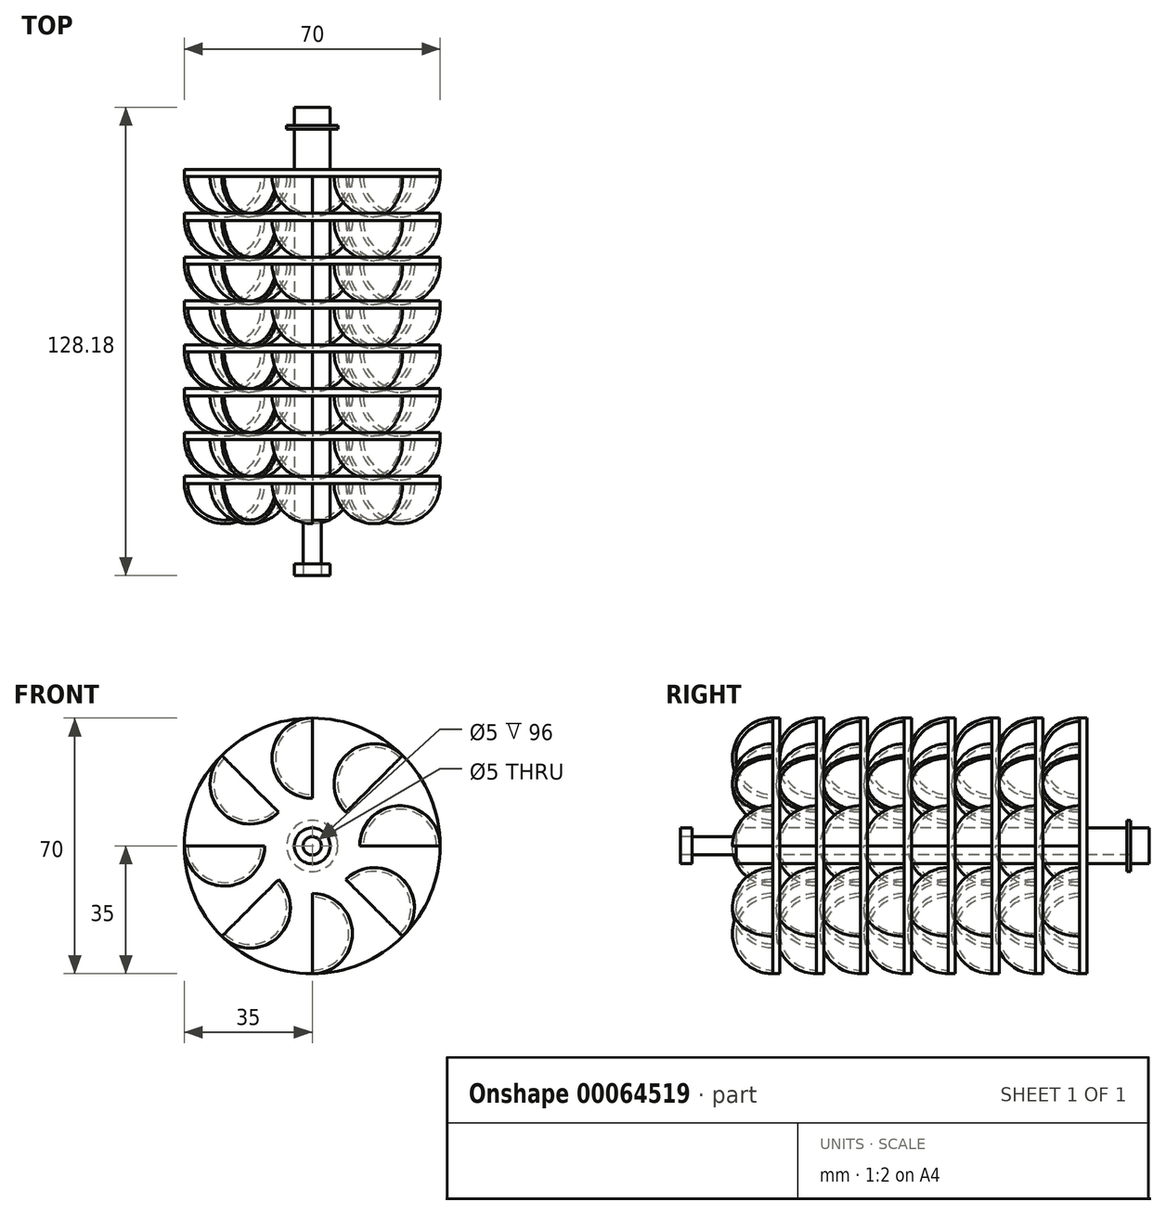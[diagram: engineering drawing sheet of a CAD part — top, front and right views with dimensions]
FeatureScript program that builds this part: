
annotation { "Feature Type Name" : "Feature", "Feature Type Description" : "" }
export const myFeature = defineFeature(function(context is Context, id is Id, definition is map)
    precondition{}
    {
        {
            var Q0;
            Q0=qCreatedBy(makeId("Right.planeOp"),FACE);
            var sketch = newSketch(context, id + "F0", { "sketchPlane" : qUnion([Q0])});
            skArc(sketch, "E0", {"start": v(0, 10) * mm, "mid": v(-7.07, 7.07) * mm, "end": v(-10, 0) * mm});
            skLineSegment(sketch, "E1", {"start": v(-10, 0) * mm, "end": v(0, 0) * mm});
            skLineSegment(sketch, "E2", {"start": v(0, 10) * mm, "end": v(0, 0) * mm});
            skArc(sketch, "E3", {"start": v(0, 11) * mm, "mid": v(-7.78, 7.78) * mm, "end": v(-11, 0) * mm});
            skLineSegment(sketch, "E4", {"start": v(0, 10) * mm, "end": v(0, 11) * mm});
            skLineSegment(sketch, "E5", {"start": v(-11, 0) * mm, "end": v(-10, 0) * mm});
            skSolve(sketch);
        }
        {
            var Q0;
            Q0=makeQuery(id+"F0.imprint","IMPRINT",FACE,{"disambiguationData":[TD([[makeQuery(id+"F0.imprint","IMPRINT",EDGE,{"derivedFrom":sQuery(id+"F0.wireOp",EDGE,"E0")}),-1.0]])]});
            var Q1;
            Q1=sQuery(id+"F0.wireOp",EDGE,"E0");
            var Q2;
            Q2=sQuery(id+"F0.wireOp",EDGE,"E1");
            revolve(context, id + "F1", {"entities" : qUnion([Q0]), "surfaceEntities" : qUnion([Q1]), "axis" : qUnion([Q2]), "revolveType" : RevolveType.TWO_DIRECTIONS, "angle" : 90 * degree, "angleBack" : 270 * degree});
        }
        {
            var Q0;
            Q0=makeQuery(id+"F1.opRevolve","SWEPT_BODY",BODY,{"disambiguationData":[OSD([sQuery(id+"F0.wireOp",EDGE,"E0"),sQuery(id+"F0.wireOp",EDGE,"E3"),sQuery(id+"F0.wireOp",EDGE,"E4"),sQuery(id+"F0.wireOp",EDGE,"E5")])]});
            transform(context, id + "F2", {"entities" : qUnion([Q0]), "transformType" : TransformType.TRANSLATION_3D, "dx" : 24 * mm, "dy" : 0 * mm, "dz" : 0 * mm, "makeCopy" : false});
        }
        {
            var Q0;
            Q0=qCreatedBy(makeId("Right.planeOp"),FACE);
            var sketch = newSketch(context, id + "F3", { "sketchPlane" : qUnion([Q0])});
            skLineSegment(sketch, "E6", {"start": v(-12, 0) * mm, "end": v(0, 0) * mm});
            skLineSegment(sketch, "E7", {"start": v(0, 0) * mm, "end": v(10, 0) * mm});
            skLineSegment(sketch, "E8", {"start": v(0, 0) * mm, "end": v(0, 35) * mm});
            skLineSegment(sketch, "E9.bottom", {"start": v(-2, 0) * mm, "end": v(0, 0) * mm});
            skLineSegment(sketch, "E9.top", {"start": v(-2, 35) * mm, "end": v(0, 35) * mm});
            skLineSegment(sketch, "E9.right", {"start": v(-2, 0) * mm, "end": v(-2, 35) * mm});
            skLineSegment(sketch, "E10", {"start": v(-24, 4.9) * mm, "end": v(0, 4.9) * mm});
            skLineSegment(sketch, "E11", {"start": v(0, 4.9) * mm, "end": v(10, 4.9) * mm});
            skLineSegment(sketch, "E12", {"start": v(-2, 4.9) * mm, "end": v(-2, 0) * mm});
            skLineSegment(sketch, "E13", {"start": v(0, 4.9) * mm, "end": v(0, 0) * mm});
            skLineSegment(sketch, "E14", {"start": v(22, 0) * mm, "end": v(34, 0) * mm});
            skLineSegment(sketch, "E15", {"start": v(34, 0) * mm, "end": v(46, 0) * mm});
            skLineSegment(sketch, "E16", {"start": v(-12, 0) * mm, "end": v(-24, 0) * mm});
            skLineSegment(sketch, "E17", {"start": v(-24, 0) * mm, "end": v(-36, 0) * mm});
            skLineSegment(sketch, "E18", {"start": v(-36, 0) * mm, "end": v(-48, 0) * mm});
            skLineSegment(sketch, "E19", {"start": v(10, 0) * mm, "end": v(22, 0) * mm});
            skLineSegment(sketch, "E20", {"start": v(-24, 4.9) * mm, "end": v(-24, 4.9) * mm});
            skLineSegment(sketch, "E21", {"start": v(10, 4.9) * mm, "end": v(22, 4.9) * mm});
            skLineSegment(sketch, "E22", {"start": v(-24, 4.9) * mm, "end": v(-36, 4.9) * mm});
            skLineSegment(sketch, "E23", {"start": v(-36, 0) * mm, "end": v(-36, 4.9) * mm});
            skLineSegment(sketch, "E24", {"start": v(46, 0) * mm, "end": v(65, 0) * mm});
            skLineSegment(sketch, "E25", {"start": v(65, 0) * mm, "end": v(77, 0) * mm});
            skLineSegment(sketch, "E26", {"start": v(-48, 0) * mm, "end": v(-60, 0) * mm});
            skLineSegment(sketch, "E27", {"start": v(-36, 0) * mm, "end": v(-36, 2.5) * mm});
            skLineSegment(sketch, "E28", {"start": v(-36, 2.5) * mm, "end": v(22, 2.5) * mm});
            skLineSegment(sketch, "E29", {"start": v(-36, 0) * mm, "end": v(-38, 0) * mm});
            skLineSegment(sketch, "E30", {"start": v(10, 4.9) * mm, "end": v(10, 0) * mm});
            skLineSegment(sketch, "E31", {"start": v(10, 0) * mm, "end": v(10, 35) * mm});
            skLineSegment(sketch, "E32", {"start": v(10, 35) * mm, "end": v(12, 35) * mm});
            skLineSegment(sketch, "E33", {"start": v(12, 35) * mm, "end": v(12, 0) * mm});
            skLineSegment(sketch, "E34", {"start": v(22, 0) * mm, "end": v(22, 35) * mm});
            skLineSegment(sketch, "E35", {"start": v(22, 35) * mm, "end": v(24, 35) * mm});
            skLineSegment(sketch, "E36", {"start": v(24, 35) * mm, "end": v(24, 0) * mm});
            skLineSegment(sketch, "E37", {"start": v(34, 0) * mm, "end": v(34, 35) * mm});
            skLineSegment(sketch, "E38", {"start": v(34, 35) * mm, "end": v(36, 35) * mm});
            skLineSegment(sketch, "E39", {"start": v(36, 35) * mm, "end": v(36, 0) * mm});
            skLineSegment(sketch, "E40", {"start": v(46, 0) * mm, "end": v(46, 35) * mm});
            skLineSegment(sketch, "E41", {"start": v(46, 35) * mm, "end": v(48, 35) * mm});
            skLineSegment(sketch, "E42", {"start": v(48, 35) * mm, "end": v(48, 0) * mm});
            skLineSegment(sketch, "E43", {"start": v(22, 4.9) * mm, "end": v(34, 4.9) * mm});
            skLineSegment(sketch, "E44", {"start": v(34, 4.9) * mm, "end": v(46, 4.9) * mm});
            skLineSegment(sketch, "E45", {"start": v(46, 4.9) * mm, "end": v(65, 4.9) * mm});
            skLineSegment(sketch, "E46", {"start": v(65, 4.9) * mm, "end": v(65, 0) * mm});
            skLineSegment(sketch, "E47", {"start": v(22, 2.5) * mm, "end": v(48, 2.5) * mm});
            skLineSegment(sketch, "E48", {"start": v(-12, 35) * mm, "end": v(-14, 35) * mm});
            skLineSegment(sketch, "E49", {"start": v(-14, 35) * mm, "end": v(-14, 0) * mm});
            skLineSegment(sketch, "E50", {"start": v(-24, 0) * mm, "end": v(-24, 35) * mm});
            skLineSegment(sketch, "E51", {"start": v(-24, 35) * mm, "end": v(-26, 35) * mm});
            skLineSegment(sketch, "E52", {"start": v(-26, 35) * mm, "end": v(-26, 0) * mm});
            skLineSegment(sketch, "E53", {"start": v(-36, 0) * mm, "end": v(-36, 35) * mm});
            skLineSegment(sketch, "E54", {"start": v(-36, 35) * mm, "end": v(-38, 35) * mm});
            skLineSegment(sketch, "E55", {"start": v(-38, 35) * mm, "end": v(-38, 0) * mm});
            skLineSegment(sketch, "E56", {"start": v(-36, 4.9) * mm, "end": v(-48, 4.9) * mm});
            skLineSegment(sketch, "E57", {"start": v(-48, 4.9) * mm, "end": v(-60, 4.9) * mm});
            skLineSegment(sketch, "E58", {"start": v(-60, 4.9) * mm, "end": v(-60, 0) * mm});
            skLineSegment(sketch, "E59", {"start": v(-36, 2.5) * mm, "end": v(-60, 2.5) * mm});
            skLineSegment(sketch, "E60", {"start": v(-60, 0) * mm, "end": v(-60, 2.5) * mm});
            skLineSegment(sketch, "E61", {"start": v(-2, 4.9) * mm, "end": v(0, 4.9) * mm});
            skLineSegment(sketch, "E62", {"start": v(0, 0) * mm, "end": v(-2, 0) * mm});
            skLineSegment(sketch, "E63", {"start": v(10, 0) * mm, "end": v(-2, 0) * mm});
            skLineSegment(sketch, "E64", {"start": v(10, 4.9) * mm, "end": v(-2, 4.9) * mm});
            skLineSegment(sketch, "E65", {"start": v(22, 2.5) * mm, "end": v(12, 2.5) * mm});
            skLineSegment(sketch, "E66", {"start": v(-2, 4.9) * mm, "end": v(10, 4.9) * mm});
            skLineSegment(sketch, "E67", {"start": v(-60, 4.9) * mm, "end": v(-63.18, 4.9) * mm});
            skLineSegment(sketch, "E68", {"start": v(-63.18, 4.9) * mm, "end": v(-63.18, 0) * mm});
            skLineSegment(sketch, "E69", {"start": v(-63.18, 0) * mm, "end": v(-60, 0) * mm});
            skLineSegment(sketch, "E70", {"start": v(-63.18, 0) * mm, "end": v(-63.18, 2.5) * mm});
            skLineSegment(sketch, "E71", {"start": v(60, 0) * mm, "end": v(60, 7) * mm});
            skLineSegment(sketch, "E72", {"start": v(60, 7) * mm, "end": v(59, 7) * mm});
            skLineSegment(sketch, "E73", {"start": v(59, 0) * mm, "end": v(59, 7) * mm});
            skLineSegment(sketch, "E74", {"start": v(-12, 35) * mm, "end": v(-12, 0) * mm});
            skPoint(sketch, "E75", {"position": v(65, 2.5) * mm});
            skLineSegment(sketch, "E76", {"start": v(48, 2.5) * mm, "end": v(65, 2.5) * mm});
            skLineSegment(sketch, "E77", {"start": v(65, 2.5) * mm, "end": v(65, 0) * mm});
            skLineSegment(sketch, "E78", {"start": v(-60, 2.5) * mm, "end": v(-63.18, 2.5) * mm});
            skLineSegment(sketch, "E79", {"start": v(-60, 0) * mm, "end": v(-38, 0) * mm});
            skLineSegment(sketch, "E80", {"start": v(-60, 4.9) * mm, "end": v(-36, 4.9) * mm});
            skLineSegment(sketch, "E81", {"start": v(-60, 0) * mm, "end": v(-36, 0) * mm});
            skLineSegment(sketch, "E82", {"start": v(-48, 4.9) * mm, "end": v(-48, 0) * mm});
            skSolve(sketch);
        }
        {
            var Q0;
            {var subQ5=sQuery(id+"F3.wireOp",EDGE,"E22");var subQ7=makeQuery(id+"F3.imprint","IMPRINT",VERTEX,{"derivedFrom":subQ5});Q0=makeQuery(id+"F3.imprint","IMPRINT",FACE,{"disambiguationData":[TD([[makeQuery(id+"F3.imprint","IMPRINT",EDGE,{"disambiguationData":[TD([[subQ7,-1.0]])],"derivedFrom":subQ5}),1.0]])]});}
            var Q1;
            {var subQ3=sQuery(id+"F3.wireOp",EDGE,"E51");Q1=makeQuery(id+"F3.imprint","IMPRINT",FACE,{"disambiguationData":[TD([[makeQuery(id+"F3.imprint","IMPRINT",EDGE,{"derivedFrom":subQ3}),1.0]])]});}
            var Q2;
            {var subQ0=sQuery(id+"F3.wireOp",EDGE,"E50");var subQ5=sQuery(id+"F3.wireOp",EDGE,"E28");var subQ6=makeQuery(id+"F3.imprint","INTERSECT",VERTEX,{"derivedFrom":[subQ5,subQ0]});Q2=makeQuery(id+"F3.imprint","IMPRINT",FACE,{"disambiguationData":[TD([[makeQuery(id+"F3.imprint","IMPRINT",EDGE,{"disambiguationData":[TD([[subQ6,-1.0]])],"derivedFrom":subQ5}),1.0]])]});}
            var Q3;
            {var subQ0=sQuery(id+"F3.wireOp",EDGE,"E49");var subQ1=sQuery(id+"F3.wireOp",EDGE,"E10");var subQ2=makeQuery(id+"F3.imprint","INTERSECT",VERTEX,{"derivedFrom":[subQ1,subQ0]});Q3=makeQuery(id+"F3.imprint","IMPRINT",FACE,{"disambiguationData":[TD([[makeQuery(id+"F3.imprint","IMPRINT",EDGE,{"disambiguationData":[TD([[subQ2,-1.0]])],"derivedFrom":subQ1}),-1.0]])]});}
            var Q4;
            {var subQ5=sQuery(id+"F3.wireOp",EDGE,"E48");Q4=makeQuery(id+"F3.imprint","IMPRINT",FACE,{"disambiguationData":[TD([[makeQuery(id+"F3.imprint","IMPRINT",EDGE,{"derivedFrom":subQ5}),1.0]])]});}
            var Q5;
            {var subQ0=sQuery(id+"F3.wireOp",EDGE,"E12");var subQ5=sQuery(id+"F3.wireOp",EDGE,"E28");var subQ6=makeQuery(id+"F3.imprint","INTERSECT",VERTEX,{"derivedFrom":[subQ0,subQ5]});Q5=makeQuery(id+"F3.imprint","IMPRINT",FACE,{"disambiguationData":[TD([[makeQuery(id+"F3.imprint","IMPRINT",EDGE,{"disambiguationData":[TD([[subQ6,1.0]])],"derivedFrom":subQ5}),1.0]])]});}
            var Q6;
            {var subQ1=sQuery(id+"F3.wireOp",EDGE,"E42");var subQ3=sQuery(id+"F3.wireOp",EDGE,"E45");var subQ4=makeQuery(id+"F3.imprint","INTERSECT",VERTEX,{"derivedFrom":[subQ1,subQ3]});Q6=makeQuery(id+"F3.imprint","IMPRINT",FACE,{"disambiguationData":[TD([[makeQuery(id+"F3.imprint","IMPRINT",EDGE,{"disambiguationData":[TD([[subQ4,-1.0]])],"derivedFrom":subQ3}),-1.0]])]});}
            var Q7;
            {var subQ1=sQuery(id+"F3.wireOp",EDGE,"E40");var subQ3=sQuery(id+"F3.wireOp",EDGE,"E47");var subQ4=makeQuery(id+"F3.imprint","INTERSECT",VERTEX,{"derivedFrom":[subQ1,subQ3]});Q7=makeQuery(id+"F3.imprint","IMPRINT",FACE,{"disambiguationData":[TD([[makeQuery(id+"F3.imprint","IMPRINT",EDGE,{"disambiguationData":[TD([[subQ4,-1.0]])],"derivedFrom":subQ1}),-1.0]])]});}
            var Q8;
            {var subQ0=sQuery(id+"F3.wireOp",EDGE,"E41");Q8=makeQuery(id+"F3.imprint","IMPRINT",FACE,{"disambiguationData":[TD([[makeQuery(id+"F3.imprint","IMPRINT",EDGE,{"derivedFrom":subQ0}),-1.0]])]});}
            var Q9;
            {var subQ0=sQuery(id+"F3.wireOp",EDGE,"E44");var subQ1=sQuery(id+"F3.wireOp",EDGE,"E39");var subQ2=makeQuery(id+"F3.imprint","INTERSECT",VERTEX,{"derivedFrom":[subQ1,subQ0]});Q9=makeQuery(id+"F3.imprint","IMPRINT",FACE,{"disambiguationData":[TD([[makeQuery(id+"F3.imprint","IMPRINT",EDGE,{"disambiguationData":[TD([[subQ2,-1.0]])],"derivedFrom":subQ1}),1.0]])]});}
            var Q10;
            {var subQ0=sQuery(id+"F3.wireOp",EDGE,"E44");var subQ5=sQuery(id+"F3.wireOp",EDGE,"E39");var subQ6=makeQuery(id+"F3.imprint","INTERSECT",VERTEX,{"derivedFrom":[subQ5,subQ0]});Q10=makeQuery(id+"F3.imprint","IMPRINT",FACE,{"disambiguationData":[TD([[makeQuery(id+"F3.imprint","IMPRINT",EDGE,{"disambiguationData":[TD([[subQ6,-1.0]])],"derivedFrom":subQ5}),-1.0]])]});}
            var Q11;
            {var subQ0=sQuery(id+"F3.wireOp",EDGE,"E38");Q11=makeQuery(id+"F3.imprint","IMPRINT",FACE,{"disambiguationData":[TD([[makeQuery(id+"F3.imprint","IMPRINT",EDGE,{"derivedFrom":subQ0}),-1.0]])]});}
            var Q12;
            {var subQ0=sQuery(id+"F3.wireOp",EDGE,"E43");var subQ1=sQuery(id+"F3.wireOp",EDGE,"E36");var subQ2=makeQuery(id+"F3.imprint","INTERSECT",VERTEX,{"derivedFrom":[subQ1,subQ0]});Q12=makeQuery(id+"F3.imprint","IMPRINT",FACE,{"disambiguationData":[TD([[makeQuery(id+"F3.imprint","IMPRINT",EDGE,{"disambiguationData":[TD([[subQ2,-1.0]])],"derivedFrom":subQ1}),1.0]])]});}
            var Q13;
            {var subQ0=sQuery(id+"F3.wireOp",EDGE,"E43");var subQ5=sQuery(id+"F3.wireOp",EDGE,"E36");var subQ7=makeQuery(id+"F3.imprint","INTERSECT",VERTEX,{"derivedFrom":[subQ5,subQ0]});Q13=makeQuery(id+"F3.imprint","IMPRINT",FACE,{"disambiguationData":[TD([[makeQuery(id+"F3.imprint","IMPRINT",EDGE,{"disambiguationData":[TD([[subQ7,-1.0]])],"derivedFrom":subQ5}),-1.0]])]});}
            var Q14;
            {var subQ3=sQuery(id+"F3.wireOp",EDGE,"E35");Q14=makeQuery(id+"F3.imprint","IMPRINT",FACE,{"disambiguationData":[TD([[makeQuery(id+"F3.imprint","IMPRINT",EDGE,{"derivedFrom":subQ3}),-1.0]])]});}
            var Q15;
            {var subQ5=sQuery(id+"F3.wireOp",EDGE,"E65");Q15=makeQuery(id+"F3.imprint","IMPRINT",FACE,{"disambiguationData":[TD([[makeQuery(id+"F3.imprint","IMPRINT",EDGE,{"derivedFrom":subQ5}),-1.0]])]});}
            var Q16;
            {var subQ1=sQuery(id+"F3.wireOp",EDGE,"E21");var subQ3=sQuery(id+"F3.wireOp",EDGE,"E33");var subQ4=makeQuery(id+"F3.imprint","INTERSECT",VERTEX,{"derivedFrom":[subQ1,subQ3]});Q16=makeQuery(id+"F3.imprint","IMPRINT",FACE,{"disambiguationData":[TD([[makeQuery(id+"F3.imprint","IMPRINT",EDGE,{"disambiguationData":[TD([[subQ4,1.0]])],"derivedFrom":subQ1}),-1.0]])]});}
            var Q17;
            {var subQ5=sQuery(id+"F3.wireOp",EDGE,"E32");Q17=makeQuery(id+"F3.imprint","IMPRINT",FACE,{"disambiguationData":[TD([[makeQuery(id+"F3.imprint","IMPRINT",EDGE,{"derivedFrom":subQ5}),-1.0]])]});}
            var Q18;
            {var subQ1=sQuery(id+"F3.wireOp",EDGE,"E13");var subQ3=sQuery(id+"F3.wireOp",EDGE,"E28");var subQ4=makeQuery(id+"F3.imprint","INTERSECT",VERTEX,{"derivedFrom":[subQ1,subQ3]});Q18=makeQuery(id+"F3.imprint","IMPRINT",FACE,{"disambiguationData":[TD([[makeQuery(id+"F3.imprint","IMPRINT",EDGE,{"disambiguationData":[TD([[subQ4,-1.0]])],"derivedFrom":subQ3}),1.0]])]});}
            var Q19;
            {var subQ1=sQuery(id+"F3.wireOp",EDGE,"E12");var subQ3=sQuery(id+"F3.wireOp",EDGE,"E28");var subQ4=makeQuery(id+"F3.imprint","INTERSECT",VERTEX,{"derivedFrom":[subQ1,subQ3]});Q19=makeQuery(id+"F3.imprint","IMPRINT",FACE,{"disambiguationData":[TD([[makeQuery(id+"F3.imprint","IMPRINT",EDGE,{"disambiguationData":[TD([[subQ4,-1.0]])],"derivedFrom":subQ3}),1.0]])]});}
            var Q20;
            Q20=makeQuery(id+"F3.imprint","IMPRINT",FACE,{"disambiguationData":[TD([[makeQuery(id+"F3.imprint","IMPRINT",EDGE,{"derivedFrom":sQuery(id+"F3.wireOp",EDGE,"E9.top")}),-1.0]])]});
            var Q21;
            {var subQ0=sQuery(id+"F3.wireOp",EDGE,"E46");Q21=makeQuery(id+"F3.imprint","IMPRINT",FACE,{"disambiguationData":[TD([[makeQuery(id+"F3.imprint","IMPRINT",EDGE,{"derivedFrom":subQ0}),-1.0]])]});}
            var Q22;
            {var subQ0=sQuery(id+"F3.wireOp",EDGE,"E73");var subQ1=sQuery(id+"F3.wireOp",EDGE,"E45");var subQ2=makeQuery(id+"F3.imprint","INTERSECT",VERTEX,{"derivedFrom":[subQ1,subQ0]});Q22=makeQuery(id+"F3.imprint","IMPRINT",FACE,{"disambiguationData":[TD([[makeQuery(id+"F3.imprint","IMPRINT",EDGE,{"disambiguationData":[TD([[subQ2,-1.0]])],"derivedFrom":subQ1}),-1.0]])]});}
            var Q23;
            {var subQ5=sQuery(id+"F3.wireOp",EDGE,"E72");Q23=makeQuery(id+"F3.imprint","IMPRINT",FACE,{"disambiguationData":[TD([[makeQuery(id+"F3.imprint","IMPRINT",EDGE,{"derivedFrom":subQ5}),1.0]])]});}
            var Q24;
            {var subQ3=sQuery(id+"F3.wireOp",EDGE,"E82");var subQ5=sQuery(id+"F3.wireOp",EDGE,"E80");var subQ7=makeQuery(id+"F3.imprint","INTERSECT",VERTEX,{"derivedFrom":[subQ5,subQ3]});Q24=makeQuery(id+"F3.imprint","IMPRINT",FACE,{"disambiguationData":[TD([[makeQuery(id+"F3.imprint","IMPRINT",EDGE,{"disambiguationData":[TD([[subQ7,-1.0]])],"derivedFrom":subQ3}),-1.0]])]});}
            var Q25;
            {var subQ3=sQuery(id+"F3.wireOp",EDGE,"E82");var subQ5=sQuery(id+"F3.wireOp",EDGE,"E80");var subQ7=makeQuery(id+"F3.imprint","INTERSECT",VERTEX,{"derivedFrom":[subQ5,subQ3]});Q25=makeQuery(id+"F3.imprint","IMPRINT",FACE,{"disambiguationData":[TD([[makeQuery(id+"F3.imprint","IMPRINT",EDGE,{"disambiguationData":[TD([[subQ7,-1.0]])],"derivedFrom":subQ3}),-1.0]])]});}
            var Q26;
            {var subQ2=sQuery(id+"F3.wireOp",EDGE,"E67");Q26=makeQuery(id+"F3.imprint","IMPRINT",FACE,{"disambiguationData":[TD([[makeQuery(id+"F3.imprint","IMPRINT",EDGE,{"derivedFrom":subQ2}),1.0]])]});}
            var Q27;
            {var subQ0=sQuery(id+"F3.wireOp",EDGE,"E80");var subQ1=sQuery(id+"F3.wireOp",EDGE,"E55");var subQ2=makeQuery(id+"F3.imprint","INTERSECT",VERTEX,{"derivedFrom":[subQ1,subQ0]});Q27=makeQuery(id+"F3.imprint","IMPRINT",FACE,{"disambiguationData":[TD([[makeQuery(id+"F3.imprint","IMPRINT",EDGE,{"disambiguationData":[TD([[subQ2,-1.0]])],"derivedFrom":subQ1}),-1.0]])]});}
            var Q28;
            {var subQ0=sQuery(id+"F3.wireOp",EDGE,"E80");var subQ5=sQuery(id+"F3.wireOp",EDGE,"E55");var subQ6=makeQuery(id+"F3.imprint","INTERSECT",VERTEX,{"derivedFrom":[subQ5,subQ0]});Q28=makeQuery(id+"F3.imprint","IMPRINT",FACE,{"disambiguationData":[TD([[makeQuery(id+"F3.imprint","IMPRINT",EDGE,{"disambiguationData":[TD([[subQ6,-1.0]])],"derivedFrom":subQ5}),1.0]])]});}
            var Q29;
            {var subQ3=sQuery(id+"F3.wireOp",EDGE,"E54");Q29=makeQuery(id+"F3.imprint","IMPRINT",FACE,{"disambiguationData":[TD([[makeQuery(id+"F3.imprint","IMPRINT",EDGE,{"derivedFrom":subQ3}),1.0]])]});}
            var Q30;
            {var subQ1=sQuery(id+"F3.wireOp",EDGE,"E22");var subQ3=sQuery(id+"F3.wireOp",EDGE,"E52");var subQ4=makeQuery(id+"F3.imprint","INTERSECT",VERTEX,{"derivedFrom":[subQ1,subQ3]});Q30=makeQuery(id+"F3.imprint","IMPRINT",FACE,{"disambiguationData":[TD([[makeQuery(id+"F3.imprint","IMPRINT",EDGE,{"disambiguationData":[TD([[subQ4,-1.0]])],"derivedFrom":subQ3}),-1.0]])]});}
            var Q31;
            Q31=sQuery(id+"F3.wireOp",EDGE,"E6");
            revolve(context, id + "F4", {"entities" : qUnion([Q0, Q1, Q2, Q3, Q4, Q5, Q6, Q7, Q8, Q9, Q10, Q11, Q12, Q13, Q14, Q15, Q16, Q17, Q18, Q19, Q20, Q21, Q22, Q23, Q24, Q25, Q26, Q27, Q28, Q29, Q30]), "axis" : qUnion([Q31]), "revolveType" : RevolveType.FULL});
        }
        {
            var Q0;
            Q0=makeQuery(id+"F1.opRevolve","SWEPT_BODY",BODY,{"disambiguationData":[OSD([sQuery(id+"F0.wireOp",EDGE,"E0"),sQuery(id+"F0.wireOp",EDGE,"E3"),sQuery(id+"F0.wireOp",EDGE,"E4"),sQuery(id+"F0.wireOp",EDGE,"E5")])]});
            var Q1;
            Q1=sQuery(id+"F3.wireOp",EDGE,"E6");
            transform(context, id + "F5", {"entities" : qUnion([Q0]), "transformType" : TransformType.ROTATION, "transformAxis" : qUnion([Q1]), "angle" : 90 * degree, "makeCopy" : true});
        }
        {
            var Q0;
            Q0=makeQuery(id+"F1.opRevolve","SWEPT_BODY",BODY,{"disambiguationData":[OSD([sQuery(id+"F0.wireOp",EDGE,"E0"),sQuery(id+"F0.wireOp",EDGE,"E3"),sQuery(id+"F0.wireOp",EDGE,"E4"),sQuery(id+"F0.wireOp",EDGE,"E5")])]});
            var Q1;
            Q1=makeQuery(id+"F5.opPattern","COPY",BODY,{"derivedFrom":makeQuery(id+"F1.opRevolve","SWEPT_BODY",BODY,{"disambiguationData":[OSD([sQuery(id+"F0.wireOp",EDGE,"E0"),sQuery(id+"F0.wireOp",EDGE,"E3"),sQuery(id+"F0.wireOp",EDGE,"E4"),sQuery(id+"F0.wireOp",EDGE,"E5")])]}),"instanceName":"1"});
            var Q2;
            Q2=sQuery(id+"F3.wireOp",EDGE,"E7");
            transform(context, id + "F6", {"entities" : qUnion([Q0, Q1]), "transformType" : TransformType.ROTATION, "transformAxis" : qUnion([Q2]), "angle" : 180 * degree, "makeCopy" : true});
        }
        {
            var Q0;
            Q0=makeQuery(id+"F1.opRevolve","SWEPT_BODY",BODY,{"disambiguationData":[OSD([sQuery(id+"F0.wireOp",EDGE,"E0"),sQuery(id+"F0.wireOp",EDGE,"E3"),sQuery(id+"F0.wireOp",EDGE,"E4"),sQuery(id+"F0.wireOp",EDGE,"E5")])]});
            var Q1;
            Q1=makeQuery(id+"F6.opPattern","COPY",BODY,{"derivedFrom":makeQuery(id+"F5.opPattern","COPY",BODY,{"derivedFrom":makeQuery(id+"F1.opRevolve","SWEPT_BODY",BODY,{"disambiguationData":[OSD([sQuery(id+"F0.wireOp",EDGE,"E0"),sQuery(id+"F0.wireOp",EDGE,"E3"),sQuery(id+"F0.wireOp",EDGE,"E4"),sQuery(id+"F0.wireOp",EDGE,"E5")])]}),"instanceName":"1"}),"instanceName":"1"});
            var Q2;
            Q2=makeQuery(id+"F6.opPattern","COPY",BODY,{"derivedFrom":makeQuery(id+"F1.opRevolve","SWEPT_BODY",BODY,{"disambiguationData":[OSD([sQuery(id+"F0.wireOp",EDGE,"E0"),sQuery(id+"F0.wireOp",EDGE,"E3"),sQuery(id+"F0.wireOp",EDGE,"E4"),sQuery(id+"F0.wireOp",EDGE,"E5")])]}),"instanceName":"1"});
            var Q3;
            Q3=makeQuery(id+"F5.opPattern","COPY",BODY,{"derivedFrom":makeQuery(id+"F1.opRevolve","SWEPT_BODY",BODY,{"disambiguationData":[OSD([sQuery(id+"F0.wireOp",EDGE,"E0"),sQuery(id+"F0.wireOp",EDGE,"E3"),sQuery(id+"F0.wireOp",EDGE,"E4"),sQuery(id+"F0.wireOp",EDGE,"E5")])]}),"instanceName":"1"});
            var Q4;
            Q4=sQuery(id+"F3.wireOp",EDGE,"E25");
            transform(context, id + "F7", {"entities" : qUnion([Q0, Q1, Q2, Q3]), "transformType" : TransformType.ROTATION, "transformAxis" : qUnion([Q4]), "angle" : 45 * degree, "makeCopy" : true});
        }
        {
            var Q0;
            Q0=makeQuery(id+"F1.opRevolve","SWEPT_BODY",BODY,{"disambiguationData":[OSD([sQuery(id+"F0.wireOp",EDGE,"E0"),sQuery(id+"F0.wireOp",EDGE,"E3"),sQuery(id+"F0.wireOp",EDGE,"E4"),sQuery(id+"F0.wireOp",EDGE,"E5")])]});
            var Q1;
            Q1=makeQuery(id+"F7.opPattern","COPY",BODY,{"derivedFrom":makeQuery(id+"F1.opRevolve","SWEPT_BODY",BODY,{"disambiguationData":[OSD([sQuery(id+"F0.wireOp",EDGE,"E0"),sQuery(id+"F0.wireOp",EDGE,"E3"),sQuery(id+"F0.wireOp",EDGE,"E4"),sQuery(id+"F0.wireOp",EDGE,"E5")])]}),"instanceName":"1"});
            var Q2;
            Q2=makeQuery(id+"F5.opPattern","COPY",BODY,{"derivedFrom":makeQuery(id+"F1.opRevolve","SWEPT_BODY",BODY,{"disambiguationData":[OSD([sQuery(id+"F0.wireOp",EDGE,"E0"),sQuery(id+"F0.wireOp",EDGE,"E3"),sQuery(id+"F0.wireOp",EDGE,"E4"),sQuery(id+"F0.wireOp",EDGE,"E5")])]}),"instanceName":"1"});
            var Q3;
            Q3=makeQuery(id+"F7.opPattern","COPY",BODY,{"derivedFrom":makeQuery(id+"F5.opPattern","COPY",BODY,{"derivedFrom":makeQuery(id+"F1.opRevolve","SWEPT_BODY",BODY,{"disambiguationData":[OSD([sQuery(id+"F0.wireOp",EDGE,"E0"),sQuery(id+"F0.wireOp",EDGE,"E3"),sQuery(id+"F0.wireOp",EDGE,"E4"),sQuery(id+"F0.wireOp",EDGE,"E5")])]}),"instanceName":"1"}),"instanceName":"1"});
            var Q4;
            Q4=makeQuery(id+"F6.opPattern","COPY",BODY,{"derivedFrom":makeQuery(id+"F1.opRevolve","SWEPT_BODY",BODY,{"disambiguationData":[OSD([sQuery(id+"F0.wireOp",EDGE,"E0"),sQuery(id+"F0.wireOp",EDGE,"E3"),sQuery(id+"F0.wireOp",EDGE,"E4"),sQuery(id+"F0.wireOp",EDGE,"E5")])]}),"instanceName":"1"});
            var Q5;
            Q5=makeQuery(id+"F7.opPattern","COPY",BODY,{"derivedFrom":makeQuery(id+"F6.opPattern","COPY",BODY,{"derivedFrom":makeQuery(id+"F1.opRevolve","SWEPT_BODY",BODY,{"disambiguationData":[OSD([sQuery(id+"F0.wireOp",EDGE,"E0"),sQuery(id+"F0.wireOp",EDGE,"E3"),sQuery(id+"F0.wireOp",EDGE,"E4"),sQuery(id+"F0.wireOp",EDGE,"E5")])]}),"instanceName":"1"}),"instanceName":"1"});
            var Q6;
            Q6=makeQuery(id+"F6.opPattern","COPY",BODY,{"derivedFrom":makeQuery(id+"F5.opPattern","COPY",BODY,{"derivedFrom":makeQuery(id+"F1.opRevolve","SWEPT_BODY",BODY,{"disambiguationData":[OSD([sQuery(id+"F0.wireOp",EDGE,"E0"),sQuery(id+"F0.wireOp",EDGE,"E3"),sQuery(id+"F0.wireOp",EDGE,"E4"),sQuery(id+"F0.wireOp",EDGE,"E5")])]}),"instanceName":"1"}),"instanceName":"1"});
            var Q7;
            Q7=makeQuery(id+"F7.opPattern","COPY",BODY,{"derivedFrom":makeQuery(id+"F6.opPattern","COPY",BODY,{"derivedFrom":makeQuery(id+"F5.opPattern","COPY",BODY,{"derivedFrom":makeQuery(id+"F1.opRevolve","SWEPT_BODY",BODY,{"disambiguationData":[OSD([sQuery(id+"F0.wireOp",EDGE,"E0"),sQuery(id+"F0.wireOp",EDGE,"E3"),sQuery(id+"F0.wireOp",EDGE,"E4"),sQuery(id+"F0.wireOp",EDGE,"E5")])]}),"instanceName":"1"}),"instanceName":"1"}),"instanceName":"1"});
            var Q8;
            Q8=sQuery(id+"F3.wireOp",VERTEX,"E8.start");
            var Q9;
            Q9=sQuery(id+"F3.wireOp",VERTEX,"E62.end");
            transform(context, id + "F8", {"entities" : qUnion([Q0, Q1, Q2, Q3, Q4, Q5, Q6, Q7]), "transformType" : TransformType.TRANSLATION_ENTITY, "oppositeDirectionEntity" : false, "transformLine" : qUnion([Q8, Q9]), "makeCopy" : false});
        }
        {
            var Q0;
            Q0=makeQuery(id+"F7.opPattern","COPY",BODY,{"derivedFrom":makeQuery(id+"F5.opPattern","COPY",BODY,{"derivedFrom":makeQuery(id+"F1.opRevolve","SWEPT_BODY",BODY,{"disambiguationData":[OSD([sQuery(id+"F0.wireOp",EDGE,"E0"),sQuery(id+"F0.wireOp",EDGE,"E3"),sQuery(id+"F0.wireOp",EDGE,"E4"),sQuery(id+"F0.wireOp",EDGE,"E5")])]}),"instanceName":"1"}),"instanceName":"1"});
            var Q1;
            Q1=makeQuery(id+"F5.opPattern","COPY",BODY,{"derivedFrom":makeQuery(id+"F1.opRevolve","SWEPT_BODY",BODY,{"disambiguationData":[OSD([sQuery(id+"F0.wireOp",EDGE,"E0"),sQuery(id+"F0.wireOp",EDGE,"E3"),sQuery(id+"F0.wireOp",EDGE,"E4"),sQuery(id+"F0.wireOp",EDGE,"E5")])]}),"instanceName":"1"});
            var Q2;
            Q2=makeQuery(id+"F7.opPattern","COPY",BODY,{"derivedFrom":makeQuery(id+"F1.opRevolve","SWEPT_BODY",BODY,{"disambiguationData":[OSD([sQuery(id+"F0.wireOp",EDGE,"E0"),sQuery(id+"F0.wireOp",EDGE,"E3"),sQuery(id+"F0.wireOp",EDGE,"E4"),sQuery(id+"F0.wireOp",EDGE,"E5")])]}),"instanceName":"1"});
            var Q3;
            Q3=makeQuery(id+"F1.opRevolve","SWEPT_BODY",BODY,{"disambiguationData":[OSD([sQuery(id+"F0.wireOp",EDGE,"E0"),sQuery(id+"F0.wireOp",EDGE,"E3"),sQuery(id+"F0.wireOp",EDGE,"E4"),sQuery(id+"F0.wireOp",EDGE,"E5")])]});
            var Q4;
            Q4=makeQuery(id+"F7.opPattern","COPY",BODY,{"derivedFrom":makeQuery(id+"F6.opPattern","COPY",BODY,{"derivedFrom":makeQuery(id+"F5.opPattern","COPY",BODY,{"derivedFrom":makeQuery(id+"F1.opRevolve","SWEPT_BODY",BODY,{"disambiguationData":[OSD([sQuery(id+"F0.wireOp",EDGE,"E0"),sQuery(id+"F0.wireOp",EDGE,"E3"),sQuery(id+"F0.wireOp",EDGE,"E4"),sQuery(id+"F0.wireOp",EDGE,"E5")])]}),"instanceName":"1"}),"instanceName":"1"}),"instanceName":"1"});
            var Q5;
            Q5=makeQuery(id+"F6.opPattern","COPY",BODY,{"derivedFrom":makeQuery(id+"F5.opPattern","COPY",BODY,{"derivedFrom":makeQuery(id+"F1.opRevolve","SWEPT_BODY",BODY,{"disambiguationData":[OSD([sQuery(id+"F0.wireOp",EDGE,"E0"),sQuery(id+"F0.wireOp",EDGE,"E3"),sQuery(id+"F0.wireOp",EDGE,"E4"),sQuery(id+"F0.wireOp",EDGE,"E5")])]}),"instanceName":"1"}),"instanceName":"1"});
            var Q6;
            Q6=makeQuery(id+"F7.opPattern","COPY",BODY,{"derivedFrom":makeQuery(id+"F6.opPattern","COPY",BODY,{"derivedFrom":makeQuery(id+"F1.opRevolve","SWEPT_BODY",BODY,{"disambiguationData":[OSD([sQuery(id+"F0.wireOp",EDGE,"E0"),sQuery(id+"F0.wireOp",EDGE,"E3"),sQuery(id+"F0.wireOp",EDGE,"E4"),sQuery(id+"F0.wireOp",EDGE,"E5")])]}),"instanceName":"1"}),"instanceName":"1"});
            var Q7;
            Q7=makeQuery(id+"F6.opPattern","COPY",BODY,{"derivedFrom":makeQuery(id+"F1.opRevolve","SWEPT_BODY",BODY,{"disambiguationData":[OSD([sQuery(id+"F0.wireOp",EDGE,"E0"),sQuery(id+"F0.wireOp",EDGE,"E3"),sQuery(id+"F0.wireOp",EDGE,"E4"),sQuery(id+"F0.wireOp",EDGE,"E5")])]}),"instanceName":"1"});
            var Q8;
            Q8=sQuery(id+"F3.wireOp",VERTEX,"E9.right.start");
            var Q9;
            Q9=sQuery(id+"F3.wireOp",VERTEX,"E49.end");
            transform(context, id + "F9", {"entities" : qUnion([Q0, Q1, Q2, Q3, Q4, Q5, Q6, Q7]), "transformType" : TransformType.TRANSLATION_ENTITY, "oppositeDirectionEntity" : false, "transformLine" : qUnion([Q8, Q9]), "makeCopy" : true});
        }
        {
            var Q0;
            Q0=makeQuery(id+"F6.opPattern","COPY",BODY,{"derivedFrom":makeQuery(id+"F1.opRevolve","SWEPT_BODY",BODY,{"disambiguationData":[OSD([sQuery(id+"F0.wireOp",EDGE,"E0"),sQuery(id+"F0.wireOp",EDGE,"E3"),sQuery(id+"F0.wireOp",EDGE,"E4"),sQuery(id+"F0.wireOp",EDGE,"E5")])]}),"instanceName":"1"});
            var Q1;
            Q1=makeQuery(id+"F7.opPattern","COPY",BODY,{"derivedFrom":makeQuery(id+"F5.opPattern","COPY",BODY,{"derivedFrom":makeQuery(id+"F1.opRevolve","SWEPT_BODY",BODY,{"disambiguationData":[OSD([sQuery(id+"F0.wireOp",EDGE,"E0"),sQuery(id+"F0.wireOp",EDGE,"E3"),sQuery(id+"F0.wireOp",EDGE,"E4"),sQuery(id+"F0.wireOp",EDGE,"E5")])]}),"instanceName":"1"}),"instanceName":"1"});
            var Q2;
            Q2=makeQuery(id+"F5.opPattern","COPY",BODY,{"derivedFrom":makeQuery(id+"F1.opRevolve","SWEPT_BODY",BODY,{"disambiguationData":[OSD([sQuery(id+"F0.wireOp",EDGE,"E0"),sQuery(id+"F0.wireOp",EDGE,"E3"),sQuery(id+"F0.wireOp",EDGE,"E4"),sQuery(id+"F0.wireOp",EDGE,"E5")])]}),"instanceName":"1"});
            var Q3;
            Q3=makeQuery(id+"F7.opPattern","COPY",BODY,{"derivedFrom":makeQuery(id+"F1.opRevolve","SWEPT_BODY",BODY,{"disambiguationData":[OSD([sQuery(id+"F0.wireOp",EDGE,"E0"),sQuery(id+"F0.wireOp",EDGE,"E3"),sQuery(id+"F0.wireOp",EDGE,"E4"),sQuery(id+"F0.wireOp",EDGE,"E5")])]}),"instanceName":"1"});
            var Q4;
            Q4=makeQuery(id+"F1.opRevolve","SWEPT_BODY",BODY,{"disambiguationData":[OSD([sQuery(id+"F0.wireOp",EDGE,"E0"),sQuery(id+"F0.wireOp",EDGE,"E3"),sQuery(id+"F0.wireOp",EDGE,"E4"),sQuery(id+"F0.wireOp",EDGE,"E5")])]});
            var Q5;
            Q5=makeQuery(id+"F7.opPattern","COPY",BODY,{"derivedFrom":makeQuery(id+"F6.opPattern","COPY",BODY,{"derivedFrom":makeQuery(id+"F5.opPattern","COPY",BODY,{"derivedFrom":makeQuery(id+"F1.opRevolve","SWEPT_BODY",BODY,{"disambiguationData":[OSD([sQuery(id+"F0.wireOp",EDGE,"E0"),sQuery(id+"F0.wireOp",EDGE,"E3"),sQuery(id+"F0.wireOp",EDGE,"E4"),sQuery(id+"F0.wireOp",EDGE,"E5")])]}),"instanceName":"1"}),"instanceName":"1"}),"instanceName":"1"});
            var Q6;
            Q6=makeQuery(id+"F6.opPattern","COPY",BODY,{"derivedFrom":makeQuery(id+"F5.opPattern","COPY",BODY,{"derivedFrom":makeQuery(id+"F1.opRevolve","SWEPT_BODY",BODY,{"disambiguationData":[OSD([sQuery(id+"F0.wireOp",EDGE,"E0"),sQuery(id+"F0.wireOp",EDGE,"E3"),sQuery(id+"F0.wireOp",EDGE,"E4"),sQuery(id+"F0.wireOp",EDGE,"E5")])]}),"instanceName":"1"}),"instanceName":"1"});
            var Q7;
            Q7=makeQuery(id+"F7.opPattern","COPY",BODY,{"derivedFrom":makeQuery(id+"F6.opPattern","COPY",BODY,{"derivedFrom":makeQuery(id+"F1.opRevolve","SWEPT_BODY",BODY,{"disambiguationData":[OSD([sQuery(id+"F0.wireOp",EDGE,"E0"),sQuery(id+"F0.wireOp",EDGE,"E3"),sQuery(id+"F0.wireOp",EDGE,"E4"),sQuery(id+"F0.wireOp",EDGE,"E5")])]}),"instanceName":"1"}),"instanceName":"1"});
            var Q8;
            Q8=makeQuery(id+"F9.opPattern","COPY",BODY,{"derivedFrom":makeQuery(id+"F7.opPattern","COPY",BODY,{"derivedFrom":makeQuery(id+"F5.opPattern","COPY",BODY,{"derivedFrom":makeQuery(id+"F1.opRevolve","SWEPT_BODY",BODY,{"disambiguationData":[OSD([sQuery(id+"F0.wireOp",EDGE,"E0"),sQuery(id+"F0.wireOp",EDGE,"E3"),sQuery(id+"F0.wireOp",EDGE,"E4"),sQuery(id+"F0.wireOp",EDGE,"E5")])]}),"instanceName":"1"}),"instanceName":"1"}),"instanceName":"1"});
            var Q9;
            Q9=makeQuery(id+"F9.opPattern","COPY",BODY,{"derivedFrom":makeQuery(id+"F5.opPattern","COPY",BODY,{"derivedFrom":makeQuery(id+"F1.opRevolve","SWEPT_BODY",BODY,{"disambiguationData":[OSD([sQuery(id+"F0.wireOp",EDGE,"E0"),sQuery(id+"F0.wireOp",EDGE,"E3"),sQuery(id+"F0.wireOp",EDGE,"E4"),sQuery(id+"F0.wireOp",EDGE,"E5")])]}),"instanceName":"1"}),"instanceName":"1"});
            var Q10;
            Q10=makeQuery(id+"F9.opPattern","COPY",BODY,{"derivedFrom":makeQuery(id+"F7.opPattern","COPY",BODY,{"derivedFrom":makeQuery(id+"F1.opRevolve","SWEPT_BODY",BODY,{"disambiguationData":[OSD([sQuery(id+"F0.wireOp",EDGE,"E0"),sQuery(id+"F0.wireOp",EDGE,"E3"),sQuery(id+"F0.wireOp",EDGE,"E4"),sQuery(id+"F0.wireOp",EDGE,"E5")])]}),"instanceName":"1"}),"instanceName":"1"});
            var Q11;
            Q11=makeQuery(id+"F9.opPattern","COPY",BODY,{"derivedFrom":makeQuery(id+"F1.opRevolve","SWEPT_BODY",BODY,{"disambiguationData":[OSD([sQuery(id+"F0.wireOp",EDGE,"E0"),sQuery(id+"F0.wireOp",EDGE,"E3"),sQuery(id+"F0.wireOp",EDGE,"E4"),sQuery(id+"F0.wireOp",EDGE,"E5")])]}),"instanceName":"1"});
            var Q12;
            Q12=makeQuery(id+"F9.opPattern","COPY",BODY,{"derivedFrom":makeQuery(id+"F7.opPattern","COPY",BODY,{"derivedFrom":makeQuery(id+"F6.opPattern","COPY",BODY,{"derivedFrom":makeQuery(id+"F5.opPattern","COPY",BODY,{"derivedFrom":makeQuery(id+"F1.opRevolve","SWEPT_BODY",BODY,{"disambiguationData":[OSD([sQuery(id+"F0.wireOp",EDGE,"E0"),sQuery(id+"F0.wireOp",EDGE,"E3"),sQuery(id+"F0.wireOp",EDGE,"E4"),sQuery(id+"F0.wireOp",EDGE,"E5")])]}),"instanceName":"1"}),"instanceName":"1"}),"instanceName":"1"}),"instanceName":"1"});
            var Q13;
            Q13=makeQuery(id+"F9.opPattern","COPY",BODY,{"derivedFrom":makeQuery(id+"F6.opPattern","COPY",BODY,{"derivedFrom":makeQuery(id+"F5.opPattern","COPY",BODY,{"derivedFrom":makeQuery(id+"F1.opRevolve","SWEPT_BODY",BODY,{"disambiguationData":[OSD([sQuery(id+"F0.wireOp",EDGE,"E0"),sQuery(id+"F0.wireOp",EDGE,"E3"),sQuery(id+"F0.wireOp",EDGE,"E4"),sQuery(id+"F0.wireOp",EDGE,"E5")])]}),"instanceName":"1"}),"instanceName":"1"}),"instanceName":"1"});
            var Q14;
            Q14=makeQuery(id+"F9.opPattern","COPY",BODY,{"derivedFrom":makeQuery(id+"F7.opPattern","COPY",BODY,{"derivedFrom":makeQuery(id+"F6.opPattern","COPY",BODY,{"derivedFrom":makeQuery(id+"F1.opRevolve","SWEPT_BODY",BODY,{"disambiguationData":[OSD([sQuery(id+"F0.wireOp",EDGE,"E0"),sQuery(id+"F0.wireOp",EDGE,"E3"),sQuery(id+"F0.wireOp",EDGE,"E4"),sQuery(id+"F0.wireOp",EDGE,"E5")])]}),"instanceName":"1"}),"instanceName":"1"}),"instanceName":"1"});
            var Q15;
            Q15=makeQuery(id+"F9.opPattern","COPY",BODY,{"derivedFrom":makeQuery(id+"F6.opPattern","COPY",BODY,{"derivedFrom":makeQuery(id+"F1.opRevolve","SWEPT_BODY",BODY,{"disambiguationData":[OSD([sQuery(id+"F0.wireOp",EDGE,"E0"),sQuery(id+"F0.wireOp",EDGE,"E3"),sQuery(id+"F0.wireOp",EDGE,"E4"),sQuery(id+"F0.wireOp",EDGE,"E5")])]}),"instanceName":"1"}),"instanceName":"1"});
            var Q16;
            Q16=sQuery(id+"F3.wireOp",VERTEX,"E9.right.start");
            var Q17;
            Q17=sQuery(id+"F3.wireOp",VERTEX,"E52.end");
            transform(context, id + "F10", {"entities" : qUnion([Q0, Q1, Q2, Q3, Q4, Q5, Q6, Q7, Q8, Q9, Q10, Q11, Q12, Q13, Q14, Q15]), "transformType" : TransformType.TRANSLATION_ENTITY, "oppositeDirectionEntity" : false, "transformLine" : qUnion([Q16, Q17]), "makeCopy" : true});
        }
        {
            var Q0;
            Q0=makeQuery(id+"F10.opPattern","COPY",BODY,{"derivedFrom":makeQuery(id+"F6.opPattern","COPY",BODY,{"derivedFrom":makeQuery(id+"F1.opRevolve","SWEPT_BODY",BODY,{"disambiguationData":[OSD([sQuery(id+"F0.wireOp",EDGE,"E0"),sQuery(id+"F0.wireOp",EDGE,"E3"),sQuery(id+"F0.wireOp",EDGE,"E4"),sQuery(id+"F0.wireOp",EDGE,"E5")])]}),"instanceName":"1"}),"instanceName":"1"});
            var Q1;
            Q1=makeQuery(id+"F10.opPattern","COPY",BODY,{"derivedFrom":makeQuery(id+"F7.opPattern","COPY",BODY,{"derivedFrom":makeQuery(id+"F5.opPattern","COPY",BODY,{"derivedFrom":makeQuery(id+"F1.opRevolve","SWEPT_BODY",BODY,{"disambiguationData":[OSD([sQuery(id+"F0.wireOp",EDGE,"E0"),sQuery(id+"F0.wireOp",EDGE,"E3"),sQuery(id+"F0.wireOp",EDGE,"E4"),sQuery(id+"F0.wireOp",EDGE,"E5")])]}),"instanceName":"1"}),"instanceName":"1"}),"instanceName":"1"});
            var Q2;
            Q2=makeQuery(id+"F10.opPattern","COPY",BODY,{"derivedFrom":makeQuery(id+"F5.opPattern","COPY",BODY,{"derivedFrom":makeQuery(id+"F1.opRevolve","SWEPT_BODY",BODY,{"disambiguationData":[OSD([sQuery(id+"F0.wireOp",EDGE,"E0"),sQuery(id+"F0.wireOp",EDGE,"E3"),sQuery(id+"F0.wireOp",EDGE,"E4"),sQuery(id+"F0.wireOp",EDGE,"E5")])]}),"instanceName":"1"}),"instanceName":"1"});
            var Q3;
            Q3=makeQuery(id+"F10.opPattern","COPY",BODY,{"derivedFrom":makeQuery(id+"F7.opPattern","COPY",BODY,{"derivedFrom":makeQuery(id+"F1.opRevolve","SWEPT_BODY",BODY,{"disambiguationData":[OSD([sQuery(id+"F0.wireOp",EDGE,"E0"),sQuery(id+"F0.wireOp",EDGE,"E3"),sQuery(id+"F0.wireOp",EDGE,"E4"),sQuery(id+"F0.wireOp",EDGE,"E5")])]}),"instanceName":"1"}),"instanceName":"1"});
            var Q4;
            Q4=makeQuery(id+"F10.opPattern","COPY",BODY,{"derivedFrom":makeQuery(id+"F1.opRevolve","SWEPT_BODY",BODY,{"disambiguationData":[OSD([sQuery(id+"F0.wireOp",EDGE,"E0"),sQuery(id+"F0.wireOp",EDGE,"E3"),sQuery(id+"F0.wireOp",EDGE,"E4"),sQuery(id+"F0.wireOp",EDGE,"E5")])]}),"instanceName":"1"});
            var Q5;
            Q5=makeQuery(id+"F10.opPattern","COPY",BODY,{"derivedFrom":makeQuery(id+"F7.opPattern","COPY",BODY,{"derivedFrom":makeQuery(id+"F6.opPattern","COPY",BODY,{"derivedFrom":makeQuery(id+"F5.opPattern","COPY",BODY,{"derivedFrom":makeQuery(id+"F1.opRevolve","SWEPT_BODY",BODY,{"disambiguationData":[OSD([sQuery(id+"F0.wireOp",EDGE,"E0"),sQuery(id+"F0.wireOp",EDGE,"E3"),sQuery(id+"F0.wireOp",EDGE,"E4"),sQuery(id+"F0.wireOp",EDGE,"E5")])]}),"instanceName":"1"}),"instanceName":"1"}),"instanceName":"1"}),"instanceName":"1"});
            var Q6;
            Q6=makeQuery(id+"F10.opPattern","COPY",BODY,{"derivedFrom":makeQuery(id+"F6.opPattern","COPY",BODY,{"derivedFrom":makeQuery(id+"F5.opPattern","COPY",BODY,{"derivedFrom":makeQuery(id+"F1.opRevolve","SWEPT_BODY",BODY,{"disambiguationData":[OSD([sQuery(id+"F0.wireOp",EDGE,"E0"),sQuery(id+"F0.wireOp",EDGE,"E3"),sQuery(id+"F0.wireOp",EDGE,"E4"),sQuery(id+"F0.wireOp",EDGE,"E5")])]}),"instanceName":"1"}),"instanceName":"1"}),"instanceName":"1"});
            var Q7;
            Q7=makeQuery(id+"F10.opPattern","COPY",BODY,{"derivedFrom":makeQuery(id+"F7.opPattern","COPY",BODY,{"derivedFrom":makeQuery(id+"F6.opPattern","COPY",BODY,{"derivedFrom":makeQuery(id+"F1.opRevolve","SWEPT_BODY",BODY,{"disambiguationData":[OSD([sQuery(id+"F0.wireOp",EDGE,"E0"),sQuery(id+"F0.wireOp",EDGE,"E3"),sQuery(id+"F0.wireOp",EDGE,"E4"),sQuery(id+"F0.wireOp",EDGE,"E5")])]}),"instanceName":"1"}),"instanceName":"1"}),"instanceName":"1"});
            var Q8;
            Q8=makeQuery(id+"F7.opPattern","COPY",BODY,{"derivedFrom":makeQuery(id+"F6.opPattern","COPY",BODY,{"derivedFrom":makeQuery(id+"F1.opRevolve","SWEPT_BODY",BODY,{"disambiguationData":[OSD([sQuery(id+"F0.wireOp",EDGE,"E0"),sQuery(id+"F0.wireOp",EDGE,"E3"),sQuery(id+"F0.wireOp",EDGE,"E4"),sQuery(id+"F0.wireOp",EDGE,"E5")])]}),"instanceName":"1"}),"instanceName":"1"});
            var Q9;
            Q9=makeQuery(id+"F6.opPattern","COPY",BODY,{"derivedFrom":makeQuery(id+"F1.opRevolve","SWEPT_BODY",BODY,{"disambiguationData":[OSD([sQuery(id+"F0.wireOp",EDGE,"E0"),sQuery(id+"F0.wireOp",EDGE,"E3"),sQuery(id+"F0.wireOp",EDGE,"E4"),sQuery(id+"F0.wireOp",EDGE,"E5")])]}),"instanceName":"1"});
            var Q10;
            Q10=makeQuery(id+"F7.opPattern","COPY",BODY,{"derivedFrom":makeQuery(id+"F5.opPattern","COPY",BODY,{"derivedFrom":makeQuery(id+"F1.opRevolve","SWEPT_BODY",BODY,{"disambiguationData":[OSD([sQuery(id+"F0.wireOp",EDGE,"E0"),sQuery(id+"F0.wireOp",EDGE,"E3"),sQuery(id+"F0.wireOp",EDGE,"E4"),sQuery(id+"F0.wireOp",EDGE,"E5")])]}),"instanceName":"1"}),"instanceName":"1"});
            var Q11;
            Q11=makeQuery(id+"F5.opPattern","COPY",BODY,{"derivedFrom":makeQuery(id+"F1.opRevolve","SWEPT_BODY",BODY,{"disambiguationData":[OSD([sQuery(id+"F0.wireOp",EDGE,"E0"),sQuery(id+"F0.wireOp",EDGE,"E3"),sQuery(id+"F0.wireOp",EDGE,"E4"),sQuery(id+"F0.wireOp",EDGE,"E5")])]}),"instanceName":"1"});
            var Q12;
            Q12=makeQuery(id+"F7.opPattern","COPY",BODY,{"derivedFrom":makeQuery(id+"F1.opRevolve","SWEPT_BODY",BODY,{"disambiguationData":[OSD([sQuery(id+"F0.wireOp",EDGE,"E0"),sQuery(id+"F0.wireOp",EDGE,"E3"),sQuery(id+"F0.wireOp",EDGE,"E4"),sQuery(id+"F0.wireOp",EDGE,"E5")])]}),"instanceName":"1"});
            var Q13;
            Q13=makeQuery(id+"F1.opRevolve","SWEPT_BODY",BODY,{"disambiguationData":[OSD([sQuery(id+"F0.wireOp",EDGE,"E0"),sQuery(id+"F0.wireOp",EDGE,"E3"),sQuery(id+"F0.wireOp",EDGE,"E4"),sQuery(id+"F0.wireOp",EDGE,"E5")])]});
            var Q14;
            Q14=makeQuery(id+"F7.opPattern","COPY",BODY,{"derivedFrom":makeQuery(id+"F6.opPattern","COPY",BODY,{"derivedFrom":makeQuery(id+"F5.opPattern","COPY",BODY,{"derivedFrom":makeQuery(id+"F1.opRevolve","SWEPT_BODY",BODY,{"disambiguationData":[OSD([sQuery(id+"F0.wireOp",EDGE,"E0"),sQuery(id+"F0.wireOp",EDGE,"E3"),sQuery(id+"F0.wireOp",EDGE,"E4"),sQuery(id+"F0.wireOp",EDGE,"E5")])]}),"instanceName":"1"}),"instanceName":"1"}),"instanceName":"1"});
            var Q15;
            Q15=makeQuery(id+"F6.opPattern","COPY",BODY,{"derivedFrom":makeQuery(id+"F5.opPattern","COPY",BODY,{"derivedFrom":makeQuery(id+"F1.opRevolve","SWEPT_BODY",BODY,{"disambiguationData":[OSD([sQuery(id+"F0.wireOp",EDGE,"E0"),sQuery(id+"F0.wireOp",EDGE,"E3"),sQuery(id+"F0.wireOp",EDGE,"E4"),sQuery(id+"F0.wireOp",EDGE,"E5")])]}),"instanceName":"1"}),"instanceName":"1"});
            var Q16;
            Q16=makeQuery(id+"F10.opPattern","COPY",BODY,{"derivedFrom":makeQuery(id+"F9.opPattern","COPY",BODY,{"derivedFrom":makeQuery(id+"F6.opPattern","COPY",BODY,{"derivedFrom":makeQuery(id+"F5.opPattern","COPY",BODY,{"derivedFrom":makeQuery(id+"F1.opRevolve","SWEPT_BODY",BODY,{"disambiguationData":[OSD([sQuery(id+"F0.wireOp",EDGE,"E0"),sQuery(id+"F0.wireOp",EDGE,"E3"),sQuery(id+"F0.wireOp",EDGE,"E4"),sQuery(id+"F0.wireOp",EDGE,"E5")])]}),"instanceName":"1"}),"instanceName":"1"}),"instanceName":"1"}),"instanceName":"1"});
            var Q17;
            Q17=makeQuery(id+"F10.opPattern","COPY",BODY,{"derivedFrom":makeQuery(id+"F9.opPattern","COPY",BODY,{"derivedFrom":makeQuery(id+"F7.opPattern","COPY",BODY,{"derivedFrom":makeQuery(id+"F6.opPattern","COPY",BODY,{"derivedFrom":makeQuery(id+"F1.opRevolve","SWEPT_BODY",BODY,{"disambiguationData":[OSD([sQuery(id+"F0.wireOp",EDGE,"E0"),sQuery(id+"F0.wireOp",EDGE,"E3"),sQuery(id+"F0.wireOp",EDGE,"E4"),sQuery(id+"F0.wireOp",EDGE,"E5")])]}),"instanceName":"1"}),"instanceName":"1"}),"instanceName":"1"}),"instanceName":"1"});
            var Q18;
            Q18=makeQuery(id+"F10.opPattern","COPY",BODY,{"derivedFrom":makeQuery(id+"F9.opPattern","COPY",BODY,{"derivedFrom":makeQuery(id+"F6.opPattern","COPY",BODY,{"derivedFrom":makeQuery(id+"F1.opRevolve","SWEPT_BODY",BODY,{"disambiguationData":[OSD([sQuery(id+"F0.wireOp",EDGE,"E0"),sQuery(id+"F0.wireOp",EDGE,"E3"),sQuery(id+"F0.wireOp",EDGE,"E4"),sQuery(id+"F0.wireOp",EDGE,"E5")])]}),"instanceName":"1"}),"instanceName":"1"}),"instanceName":"1"});
            var Q19;
            Q19=makeQuery(id+"F10.opPattern","COPY",BODY,{"derivedFrom":makeQuery(id+"F9.opPattern","COPY",BODY,{"derivedFrom":makeQuery(id+"F7.opPattern","COPY",BODY,{"derivedFrom":makeQuery(id+"F5.opPattern","COPY",BODY,{"derivedFrom":makeQuery(id+"F1.opRevolve","SWEPT_BODY",BODY,{"disambiguationData":[OSD([sQuery(id+"F0.wireOp",EDGE,"E0"),sQuery(id+"F0.wireOp",EDGE,"E3"),sQuery(id+"F0.wireOp",EDGE,"E4"),sQuery(id+"F0.wireOp",EDGE,"E5")])]}),"instanceName":"1"}),"instanceName":"1"}),"instanceName":"1"}),"instanceName":"1"});
            var Q20;
            Q20=makeQuery(id+"F10.opPattern","COPY",BODY,{"derivedFrom":makeQuery(id+"F9.opPattern","COPY",BODY,{"derivedFrom":makeQuery(id+"F5.opPattern","COPY",BODY,{"derivedFrom":makeQuery(id+"F1.opRevolve","SWEPT_BODY",BODY,{"disambiguationData":[OSD([sQuery(id+"F0.wireOp",EDGE,"E0"),sQuery(id+"F0.wireOp",EDGE,"E3"),sQuery(id+"F0.wireOp",EDGE,"E4"),sQuery(id+"F0.wireOp",EDGE,"E5")])]}),"instanceName":"1"}),"instanceName":"1"}),"instanceName":"1"});
            var Q21;
            Q21=makeQuery(id+"F10.opPattern","COPY",BODY,{"derivedFrom":makeQuery(id+"F9.opPattern","COPY",BODY,{"derivedFrom":makeQuery(id+"F7.opPattern","COPY",BODY,{"derivedFrom":makeQuery(id+"F1.opRevolve","SWEPT_BODY",BODY,{"disambiguationData":[OSD([sQuery(id+"F0.wireOp",EDGE,"E0"),sQuery(id+"F0.wireOp",EDGE,"E3"),sQuery(id+"F0.wireOp",EDGE,"E4"),sQuery(id+"F0.wireOp",EDGE,"E5")])]}),"instanceName":"1"}),"instanceName":"1"}),"instanceName":"1"});
            var Q22;
            Q22=makeQuery(id+"F10.opPattern","COPY",BODY,{"derivedFrom":makeQuery(id+"F9.opPattern","COPY",BODY,{"derivedFrom":makeQuery(id+"F1.opRevolve","SWEPT_BODY",BODY,{"disambiguationData":[OSD([sQuery(id+"F0.wireOp",EDGE,"E0"),sQuery(id+"F0.wireOp",EDGE,"E3"),sQuery(id+"F0.wireOp",EDGE,"E4"),sQuery(id+"F0.wireOp",EDGE,"E5")])]}),"instanceName":"1"}),"instanceName":"1"});
            var Q23;
            Q23=makeQuery(id+"F10.opPattern","COPY",BODY,{"derivedFrom":makeQuery(id+"F9.opPattern","COPY",BODY,{"derivedFrom":makeQuery(id+"F7.opPattern","COPY",BODY,{"derivedFrom":makeQuery(id+"F6.opPattern","COPY",BODY,{"derivedFrom":makeQuery(id+"F5.opPattern","COPY",BODY,{"derivedFrom":makeQuery(id+"F1.opRevolve","SWEPT_BODY",BODY,{"disambiguationData":[OSD([sQuery(id+"F0.wireOp",EDGE,"E0"),sQuery(id+"F0.wireOp",EDGE,"E3"),sQuery(id+"F0.wireOp",EDGE,"E4"),sQuery(id+"F0.wireOp",EDGE,"E5")])]}),"instanceName":"1"}),"instanceName":"1"}),"instanceName":"1"}),"instanceName":"1"}),"instanceName":"1"});
            var Q24;
            Q24=makeQuery(id+"F9.opPattern","COPY",BODY,{"derivedFrom":makeQuery(id+"F7.opPattern","COPY",BODY,{"derivedFrom":makeQuery(id+"F6.opPattern","COPY",BODY,{"derivedFrom":makeQuery(id+"F5.opPattern","COPY",BODY,{"derivedFrom":makeQuery(id+"F1.opRevolve","SWEPT_BODY",BODY,{"disambiguationData":[OSD([sQuery(id+"F0.wireOp",EDGE,"E0"),sQuery(id+"F0.wireOp",EDGE,"E3"),sQuery(id+"F0.wireOp",EDGE,"E4"),sQuery(id+"F0.wireOp",EDGE,"E5")])]}),"instanceName":"1"}),"instanceName":"1"}),"instanceName":"1"}),"instanceName":"1"});
            var Q25;
            Q25=makeQuery(id+"F9.opPattern","COPY",BODY,{"derivedFrom":makeQuery(id+"F6.opPattern","COPY",BODY,{"derivedFrom":makeQuery(id+"F5.opPattern","COPY",BODY,{"derivedFrom":makeQuery(id+"F1.opRevolve","SWEPT_BODY",BODY,{"disambiguationData":[OSD([sQuery(id+"F0.wireOp",EDGE,"E0"),sQuery(id+"F0.wireOp",EDGE,"E3"),sQuery(id+"F0.wireOp",EDGE,"E4"),sQuery(id+"F0.wireOp",EDGE,"E5")])]}),"instanceName":"1"}),"instanceName":"1"}),"instanceName":"1"});
            var Q26;
            Q26=makeQuery(id+"F9.opPattern","COPY",BODY,{"derivedFrom":makeQuery(id+"F7.opPattern","COPY",BODY,{"derivedFrom":makeQuery(id+"F6.opPattern","COPY",BODY,{"derivedFrom":makeQuery(id+"F1.opRevolve","SWEPT_BODY",BODY,{"disambiguationData":[OSD([sQuery(id+"F0.wireOp",EDGE,"E0"),sQuery(id+"F0.wireOp",EDGE,"E3"),sQuery(id+"F0.wireOp",EDGE,"E4"),sQuery(id+"F0.wireOp",EDGE,"E5")])]}),"instanceName":"1"}),"instanceName":"1"}),"instanceName":"1"});
            var Q27;
            Q27=makeQuery(id+"F9.opPattern","COPY",BODY,{"derivedFrom":makeQuery(id+"F6.opPattern","COPY",BODY,{"derivedFrom":makeQuery(id+"F1.opRevolve","SWEPT_BODY",BODY,{"disambiguationData":[OSD([sQuery(id+"F0.wireOp",EDGE,"E0"),sQuery(id+"F0.wireOp",EDGE,"E3"),sQuery(id+"F0.wireOp",EDGE,"E4"),sQuery(id+"F0.wireOp",EDGE,"E5")])]}),"instanceName":"1"}),"instanceName":"1"});
            var Q28;
            Q28=makeQuery(id+"F9.opPattern","COPY",BODY,{"derivedFrom":makeQuery(id+"F7.opPattern","COPY",BODY,{"derivedFrom":makeQuery(id+"F5.opPattern","COPY",BODY,{"derivedFrom":makeQuery(id+"F1.opRevolve","SWEPT_BODY",BODY,{"disambiguationData":[OSD([sQuery(id+"F0.wireOp",EDGE,"E0"),sQuery(id+"F0.wireOp",EDGE,"E3"),sQuery(id+"F0.wireOp",EDGE,"E4"),sQuery(id+"F0.wireOp",EDGE,"E5")])]}),"instanceName":"1"}),"instanceName":"1"}),"instanceName":"1"});
            var Q29;
            Q29=makeQuery(id+"F9.opPattern","COPY",BODY,{"derivedFrom":makeQuery(id+"F5.opPattern","COPY",BODY,{"derivedFrom":makeQuery(id+"F1.opRevolve","SWEPT_BODY",BODY,{"disambiguationData":[OSD([sQuery(id+"F0.wireOp",EDGE,"E0"),sQuery(id+"F0.wireOp",EDGE,"E3"),sQuery(id+"F0.wireOp",EDGE,"E4"),sQuery(id+"F0.wireOp",EDGE,"E5")])]}),"instanceName":"1"}),"instanceName":"1"});
            var Q30;
            Q30=makeQuery(id+"F9.opPattern","COPY",BODY,{"derivedFrom":makeQuery(id+"F7.opPattern","COPY",BODY,{"derivedFrom":makeQuery(id+"F1.opRevolve","SWEPT_BODY",BODY,{"disambiguationData":[OSD([sQuery(id+"F0.wireOp",EDGE,"E0"),sQuery(id+"F0.wireOp",EDGE,"E3"),sQuery(id+"F0.wireOp",EDGE,"E4"),sQuery(id+"F0.wireOp",EDGE,"E5")])]}),"instanceName":"1"}),"instanceName":"1"});
            var Q31;
            Q31=makeQuery(id+"F9.opPattern","COPY",BODY,{"derivedFrom":makeQuery(id+"F1.opRevolve","SWEPT_BODY",BODY,{"disambiguationData":[OSD([sQuery(id+"F0.wireOp",EDGE,"E0"),sQuery(id+"F0.wireOp",EDGE,"E3"),sQuery(id+"F0.wireOp",EDGE,"E4"),sQuery(id+"F0.wireOp",EDGE,"E5")])]}),"instanceName":"1"});
            var Q32;
            Q32=sQuery(id+"F3.wireOp",VERTEX,"E9.right.start");
            var Q33;
            Q33=sQuery(id+"F3.wireOp",VERTEX,"E15.end");
            transform(context, id + "F11", {"entities" : qUnion([Q0, Q1, Q2, Q3, Q4, Q5, Q6, Q7, Q8, Q9, Q10, Q11, Q12, Q13, Q14, Q15, Q16, Q17, Q18, Q19, Q20, Q21, Q22, Q23, Q24, Q25, Q26, Q27, Q28, Q29, Q30, Q31]), "transformType" : TransformType.TRANSLATION_ENTITY, "oppositeDirectionEntity" : false, "transformLine" : qUnion([Q32, Q33]), "makeCopy" : true});
        }
    });
